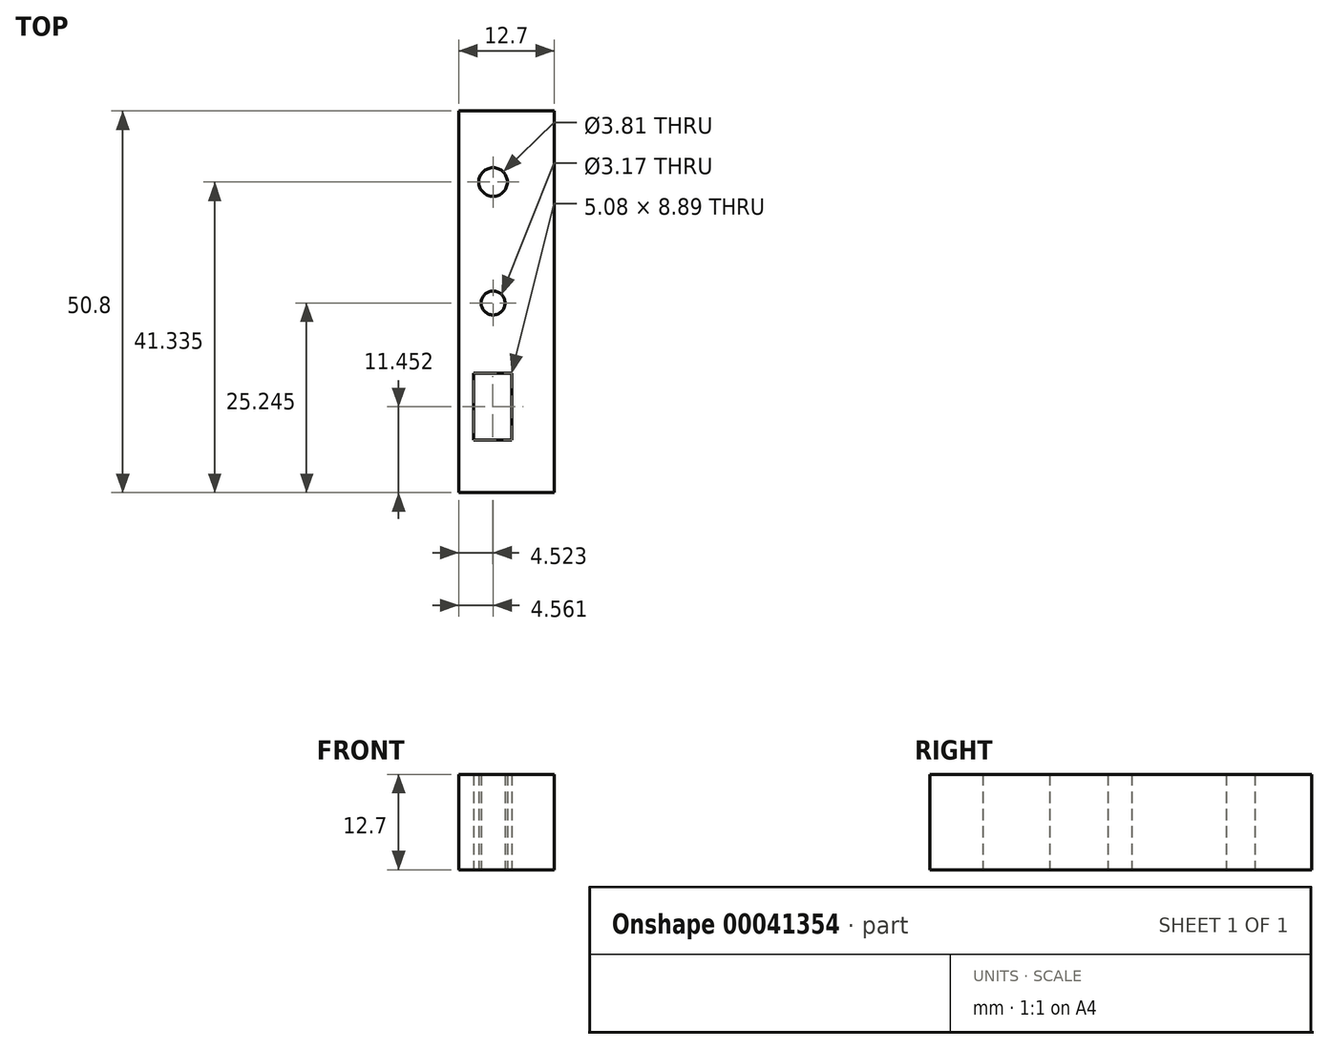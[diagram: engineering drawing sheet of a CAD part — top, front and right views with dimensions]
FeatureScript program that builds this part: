
annotation { "Feature Type Name" : "Feature", "Feature Type Description" : "" }
export const myFeature = defineFeature(function(context is Context, id is Id, definition is map)
    precondition{}
    {
        {
            var Q0;
            Q0=qCreatedBy(makeId("Top.planeOp"),FACE);
            var sketch = newSketch(context, id + "F0", { "sketchPlane" : qUnion([Q0])});
            skLineSegment(sketch, "E0.bottom", {"start": v(0, 0) * mm, "end": v(12.7, 0) * mm});
            skLineSegment(sketch, "E0.top", {"start": v(0, 50.8) * mm, "end": v(12.7, 50.8) * mm});
            skLineSegment(sketch, "E0.left", {"start": v(0, 0) * mm, "end": v(0, 50.8) * mm});
            skLineSegment(sketch, "E0.right", {"start": v(12.7, 0) * mm, "end": v(12.7, 50.8) * mm});
            skCircle(sketch, "E1", {"center": v(4.56, 41.34) * mm, "radius": 1.9 * mm});
            skCircle(sketch, "E2", {"center": v(4.56, 25.24) * mm, "radius": 1.59 * mm});
            skLineSegment(sketch, "E3.bottom", {"start": v(1.98, 15.9) * mm, "end": v(7.06, 15.9) * mm});
            skLineSegment(sketch, "E3.top", {"start": v(1.98, 7) * mm, "end": v(7.06, 7) * mm});
            skLineSegment(sketch, "E3.left", {"start": v(1.98, 15.9) * mm, "end": v(1.98, 7) * mm});
            skLineSegment(sketch, "E3.right", {"start": v(7.06, 15.9) * mm, "end": v(7.06, 7) * mm});
            skSolve(sketch);
        }
        {
            var Q0;
            Q0=makeQuery(id+"F0.imprint","IMPRINT",FACE,{"disambiguationData":[TD([[makeQuery(id+"F0.imprint","IMPRINT",EDGE,{"derivedFrom":sQuery(id+"F0.wireOp",EDGE,"E0.bottom")}),1.0]])]});
            extrude(context, id + "F1", {"entities" : qUnion([Q0]), "depth" : 12.7 * mm});
        }
    });
